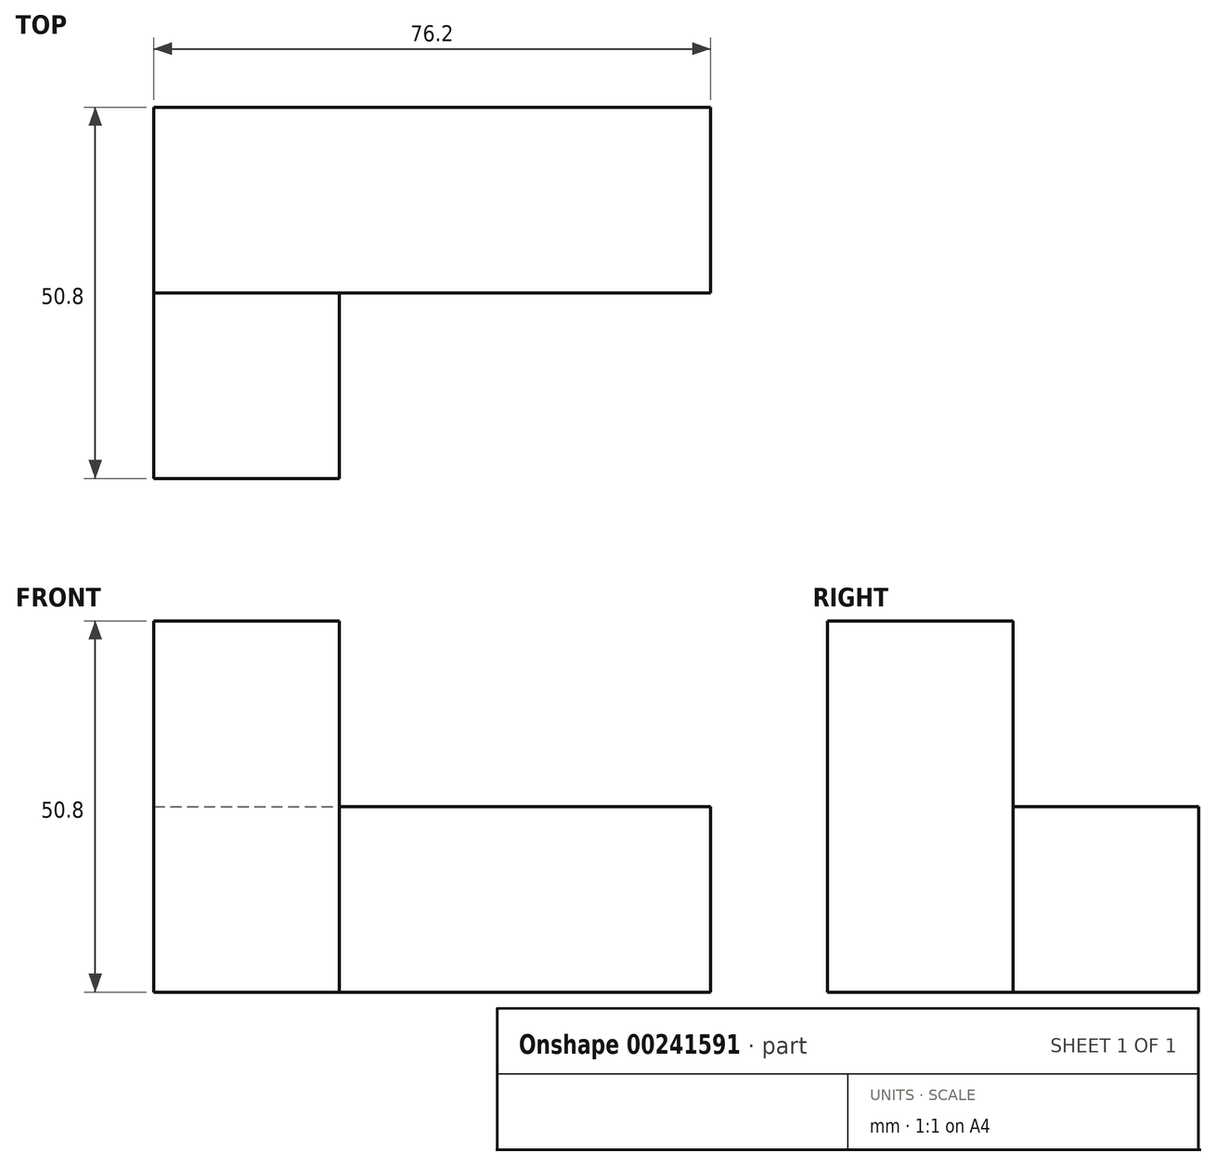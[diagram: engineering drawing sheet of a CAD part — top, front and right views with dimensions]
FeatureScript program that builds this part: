
annotation { "Feature Type Name" : "Feature", "Feature Type Description" : "" }
export const myFeature = defineFeature(function(context is Context, id is Id, definition is map)
    precondition{}
    {
        {
            var Q0;
            Q0=qCreatedBy(makeId("Front.planeOp"),FACE);
            var sketch = newSketch(context, id + "F0", { "sketchPlane" : qUnion([Q0])});
            skLineSegment(sketch, "E0.bottom", {"start": v(-33.7, 11.5) * mm, "end": v(42.5, 11.5) * mm});
            skLineSegment(sketch, "E0.top", {"start": v(-33.7, -13.9) * mm, "end": v(42.5, -13.9) * mm});
            skLineSegment(sketch, "E0.left", {"start": v(-33.7, 11.5) * mm, "end": v(-33.7, -13.9) * mm});
            skLineSegment(sketch, "E0.right", {"start": v(42.5, 11.5) * mm, "end": v(42.5, -13.9) * mm});
            skSolve(sketch);
        }
        {
            var Q0;
            Q0=makeQuery(id+"F0.imprint","IMPRINT",FACE,{"disambiguationData":[TD([[makeQuery(id+"F0.imprint","IMPRINT",EDGE,{"derivedFrom":sQuery(id+"F0.wireOp",EDGE,"E0.bottom")}),-1.0]])]});
            extrude(context, id + "F1", {"entities" : qUnion([Q0]), "depth" : 25.4 * mm});
        }
        {
            var Q0;
            Q0=makeQuery(id+"F1.opExtrude","CAP_FACE",FACE,{"disambiguationData":[OSD([sQuery(id+"F0.wireOp",EDGE,"E0.bottom"),sQuery(id+"F0.wireOp",EDGE,"E0.top"),sQuery(id+"F0.wireOp",EDGE,"E0.left"),sQuery(id+"F0.wireOp",EDGE,"E0.right")])],"isStart":false});
            var sketch = newSketch(context, id + "F2", { "sketchPlane" : qUnion([Q0])});
            skLineSegment(sketch, "E1.bottom", {"start": v(-8.3, 11.5) * mm, "end": v(-33.7, 11.5) * mm});
            skLineSegment(sketch, "E1.top", {"start": v(-8.3, -13.9) * mm, "end": v(-33.7, -13.9) * mm});
            skLineSegment(sketch, "E1.left", {"start": v(-8.3, 11.5) * mm, "end": v(-8.3, -13.9) * mm});
            skLineSegment(sketch, "E1.right", {"start": v(-33.7, 11.5) * mm, "end": v(-33.7, -13.9) * mm});
            skSolve(sketch);
        }
        {
            var Q0;
            Q0=makeQuery(id+"F2.imprint","IMPRINT",FACE,{"disambiguationData":[TD([[makeQuery(id+"F2.imprint","IMPRINT",EDGE,{"derivedFrom":sQuery(id+"F2.wireOp",EDGE,"E1.bottom")}),-1.0]])]});
            extrude(context, id + "F3", {"entities" : qUnion([Q0]), "operationType" : NewBodyOperationType.ADD, "depth" : 25.4 * mm});
        }
        {
            var Q0;
            Q0=makeQuery(id+"F3.boolean.opBoolean","MERGE",FACE,{"derivedFrom":[makeQuery(id+"F1.opExtrude","SWEPT_FACE",FACE,{"disambiguationData":[OSD([sQuery(id+"F0.wireOp",EDGE,"E0.bottom")])]}),makeQuery(id+"F3.opExtrude","SWEPT_FACE",FACE,{"disambiguationData":[OSD([sQuery(id+"F2.wireOp",EDGE,"E1.bottom")])]})]});
            var sketch = newSketch(context, id + "F4", { "sketchPlane" : qUnion([Q0])});
            skLineSegment(sketch, "E2.bottom", {"start": v(-33.7, -25.4) * mm, "end": v(-8.3, -25.4) * mm});
            skLineSegment(sketch, "E2.top", {"start": v(-33.7, -50.8) * mm, "end": v(-8.3, -50.8) * mm});
            skLineSegment(sketch, "E2.left", {"start": v(-33.7, -25.4) * mm, "end": v(-33.7, -50.8) * mm});
            skLineSegment(sketch, "E2.right", {"start": v(-8.3, -25.4) * mm, "end": v(-8.3, -50.8) * mm});
            skSolve(sketch);
        }
        {
            var Q0;
            Q0=makeQuery(id+"F4.imprint","IMPRINT",FACE,{"disambiguationData":[TD([[makeQuery(id+"F4.imprint","IMPRINT",EDGE,{"derivedFrom":sQuery(id+"F4.wireOp",EDGE,"E2.bottom")}),-1.0]])]});
            extrude(context, id + "F5", {"entities" : qUnion([Q0]), "operationType" : NewBodyOperationType.ADD, "depth" : 25.4 * mm});
        }
    });
